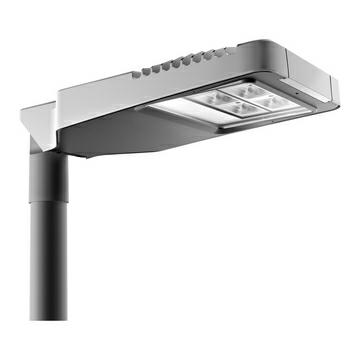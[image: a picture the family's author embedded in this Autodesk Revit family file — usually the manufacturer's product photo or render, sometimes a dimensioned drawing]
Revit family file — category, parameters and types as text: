
# Revit family: Lighting-Stradale-GEWISS-ROAD[5]MINI-LED_OTTICA_CICLOPEDONALE_CLII
name_source: partatom
category: Apparecchi per illuminazione
units: mm (PartAtom-declared; Revit-internal decimal feet)

## family parameters
Basato su piano di lavoro = No
Condiviso = No
Punto di calcolo locali = No
Quota connettore circolare = Usa diametro
Sempre verticale = Sì
Sorgente d'illuminazione = No
Taglio con vuoti quando caricato = No
Tipo di parte = Normale

## types (1)
- Lighting-Stradale-GEWISS-ROAD[5]MINI-LED_OTTICA_CICLOPEDONALE_CLII
    Alimentatore = Incluso
    Apparecchio a ridotta temperatura superficiale = -
    Applicazione = Esterno
    Cablaggio = Sezionatore
    Caratteristiche elettriche e gestione della luce = -
    Caratteristiche ottiche e illuminotecniche = -
    Catalogo = LIGHTING
    Catalogo Serie = ROAD [5]
    Certificazione DIN 18032-3 = -
    Certificazioni e classificazioni = -
    Classe fotobiologica = RG0
    Classe isolamento = II
    Classificazione: = -
    Codice Electrocod = 244C
    Codice digitale univoco (Datamatrix) = Attualmente non presente
    Colore = Grigio grafite
    Contesto = Illuminazione stradale e parcheggi
    Controllo abbagliamento e luminanza = G*3 - ULOR = 0
    Corpo = Alluminio pressofuso
    Corrente di pilotaggio. = 0,7A
    Descrizione = GWR5372MV - ROAD5 MINI CYC.V 2M 4000K 0,7A CL2
    Dispositivo di protezione = DM 10KV / CM 10KV
    Distanza minima dall'oggetto illuminato = 1M
    Durata di vita = L90B10 (Tq+25°C) = 100.000 h - L90B10 (Tq+50°C) = 75.000 h
    Efficienza luminosa (lm/W) = 72
    Finitura colore = Verniciato a polveri
    Fissaggio = Testa palo - Sbraccio
    Flusso nominale (lm) = 4700
    Frequenza nominale (Hz) = 50 / 60
    Gancio di chiusura = Maniglia frontale integrata
    Garanzia = 5 anni
    Grado di protezione = IP66
    Gruppo ottico = Riflettore in PC metallizzato
    Guarnizioni = silicone antinvecchiamento
    IDF = 3ba40a8d-00fe-4cfc-9bf5-7df65fe8b103
    IDT = 2f5e6c6e66cc494da4ced8a5a577b619
    IPEA = STRADALE = C // GRANDI AREE = B // CICLOPEDONALI = C // AREE VERDI = C // CENTRO STORICO = A
    Immagine tipo = GWR5276M.jpg
    Inclinazione = -20° ÷ +10° sbraccio - -10° ÷ +20° testa palo
    Indice di resa cromatica = CRI-70
    Informazioni generali = -
    Installazione e manutenzione = -
    LED Life Time (L80B05) = 120000H
    Lampada = LED
    Lampada: = LED
    Lumen output (lm) = 3800
    Materiali = -
    Modello = GWR5372MV
    Norma di riferimento = EN 60598-2-3, EN 60598-1 IEC/TR 62778
    Numero moduli = 2 (2x3 LED)
    Ottica = CYCLE
    Peso (kg): = 6,6
    Potenza assorbita : = 53 W @ 0.7A
    Potenza di sistema = 53W
    Produttore = GEWISS S.p.A.
    Regolazione inclinazione = -20° ÷ +10° sbraccio - -10° ÷ +20° testa palo
    Resistenza agli urti = IK08
    Resistenza al filo incandescente = -
    SEO = Stradale
    Scheda Tecnica = https://www.gewiss.com
    Schermo = Vetro piano temperato spessore 4mm
    Sistema di controllo = DALI - 5 Step
    Sostituibilità gruppo ottico = Non disponibile
    Sostituibilità piastra di cablaggio = Non disponibile
    Superficie massima esposta al vento = 0,19M2
    Superficie massima esposta al vento : = 0,15 m²
    Temperatura di colore = 4000K
    Temperatura di colore: = 4000 K (CRI>70)
    Temperatura di esercizio = -25 +50 °C
    Temperatura di stoccaggio = -
    Temperatura di utilizzo = -25 +40 °C
    Tensione = 220/240 V - 50/60 Hz - Stand alone e/o Programmabile
    Tensione di alimentazione = 220 - 240 V
    Tipo di apparecchio = Apparecchiatura stradale a LED
    Tipo di installazione e montaggio = Testa palo - Sbraccio
    Tipologia = Programmabile (5 passi)
    Tipologia sorgente luminosa = LED - Non sostituibile
    Tolleranza cromatica = SDCM = 5
    URL = https://www.gewiss.com
    Vano di alimentazione = Integrato
    Versione file RFA = 20.11
    Viti esterne = Acciaio inox

## geometry (parser evidence)
native form markers: Blend x2
no freeform markers — native parametric forms only
